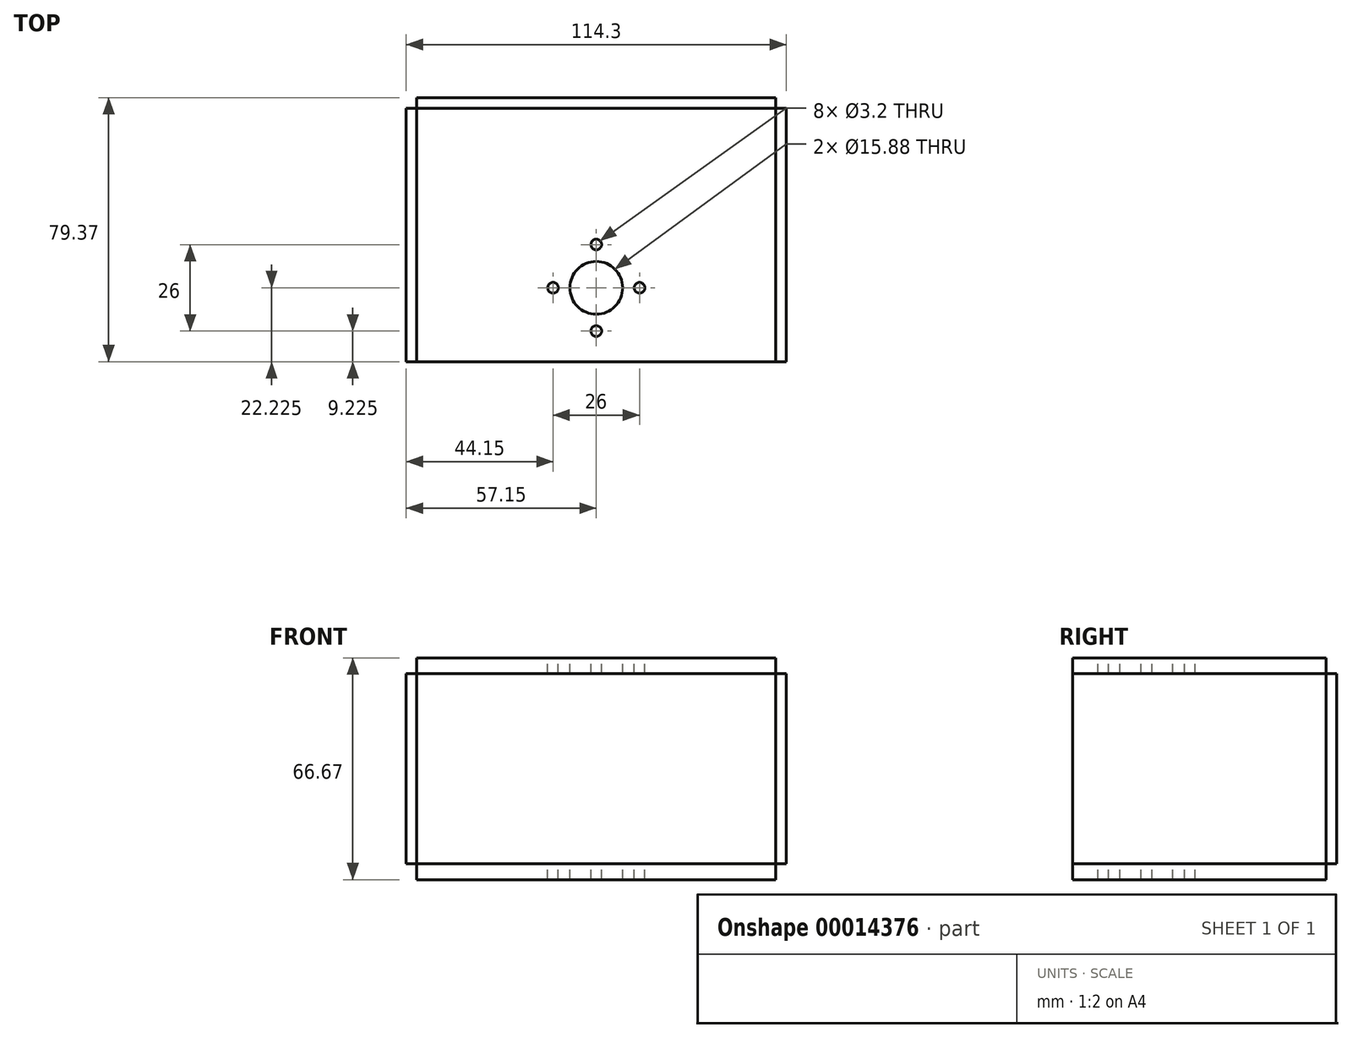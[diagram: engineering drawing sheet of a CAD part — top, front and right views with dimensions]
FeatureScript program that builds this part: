
annotation { "Feature Type Name" : "Feature", "Feature Type Description" : "" }
export const myFeature = defineFeature(function(context is Context, id is Id, definition is map)
    precondition{}
    {
        {
            var Q0;
            Q0=qCreatedBy(makeId("Top.planeOp"),FACE);
            var sketch = newSketch(context, id + "F0", { "sketchPlane" : qUnion([Q0])});
            skLineSegment(sketch, "E0.rect.bottom", {"start": v(53.97, 38.1) * mm, "end": v(-53.98, 38.1) * mm});
            skLineSegment(sketch, "E0.rect.top", {"start": v(53.98, -38.1) * mm, "end": v(-53.97, -38.1) * mm});
            skLineSegment(sketch, "E0.rect.left", {"start": v(53.97, 38.1) * mm, "end": v(53.98, -38.1) * mm});
            skLineSegment(sketch, "E0.rect.right", {"start": v(-53.98, 38.1) * mm, "end": v(-53.97, -38.1) * mm});
            skPoint(sketch, "E0.rect.middle", {"position": v(0, 0) * mm});
            skSolve(sketch);
        }
        {
            var Q0;
            Q0=qSketchRegion(id+"F0",true);
            extrude(context, id + "F1", {"entities" : qUnion([Q0]), "depth" : 4.76 * mm});
        }
        {
            var Q0;
            Q0=makeQuery(id+"F1.opExtrude","SWEPT_FACE",FACE,{"disambiguationData":[OSD([sQuery(id+"F0.wireOp",EDGE,"E0.rect.bottom")])]});
            var sketch = newSketch(context, id + "F2", { "sketchPlane" : qUnion([Q0])});
            skLineSegment(sketch, "E1.bottom", {"start": v(53.98, 0) * mm, "end": v(-53.97, 0) * mm});
            skLineSegment(sketch, "E1.top", {"start": v(53.98, -57.15) * mm, "end": v(-53.97, -57.15) * mm});
            skLineSegment(sketch, "E1.left", {"start": v(53.98, 0) * mm, "end": v(53.98, -57.15) * mm});
            skLineSegment(sketch, "E1.right", {"start": v(-53.97, 0) * mm, "end": v(-53.97, -57.15) * mm});
            skSolve(sketch);
        }
        {
            var Q0;
            Q0=qSketchRegion(id+"F2",true);
            extrude(context, id + "F3", {"entities" : qUnion([Q0]), "depth" : 3.17 * mm});
        }
        {
            var Q0;
            Q0=makeQuery(id+"F1.opExtrude","SWEPT_FACE",FACE,{"disambiguationData":[OSD([sQuery(id+"F0.wireOp",EDGE,"E0.rect.left")])]});
            var sketch = newSketch(context, id + "F4", { "sketchPlane" : qUnion([Q0])});
            skLineSegment(sketch, "E2.bottom", {"start": v(38.1, 0) * mm, "end": v(-38.1, 0) * mm});
            skLineSegment(sketch, "E2.top", {"start": v(38.1, -57.15) * mm, "end": v(-38.1, -57.15) * mm});
            skLineSegment(sketch, "E2.left", {"start": v(38.1, 0) * mm, "end": v(38.1, -57.15) * mm});
            skLineSegment(sketch, "E2.right", {"start": v(-38.1, 0) * mm, "end": v(-38.1, -57.15) * mm});
            skSolve(sketch);
        }
        {
            var Q0;
            Q0=qSketchRegion(id+"F4",true);
            extrude(context, id + "F5", {"entities" : qUnion([Q0]), "depth" : 3.17 * mm});
        }
        {
            var Q0;
            Q0=makeQuery(id+"F5.opExtrude","SWEPT_FACE",FACE,{"disambiguationData":[OSD([sQuery(id+"F4.wireOp",EDGE,"E2.top")])]});
            var sketch = newSketch(context, id + "F6", { "sketchPlane" : qUnion([Q0])});
            skLineSegment(sketch, "E3.bottom", {"start": v(53.97, -38.1) * mm, "end": v(-53.98, -38.1) * mm});
            skLineSegment(sketch, "E3.top", {"start": v(53.98, 38.1) * mm, "end": v(-53.98, 38.1) * mm});
            skLineSegment(sketch, "E3.left", {"start": v(53.97, -38.1) * mm, "end": v(53.97, 38.1) * mm});
            skLineSegment(sketch, "E3.right", {"start": v(-53.98, -38.1) * mm, "end": v(-53.98, 38.1) * mm});
            skSolve(sketch);
        }
        {
            var Q0;
            Q0=qSketchRegion(id+"F6",true);
            extrude(context, id + "F7", {"entities" : qUnion([Q0]), "depth" : 4.76 * mm});
        }
        {
            var Q0;
            Q0=makeQuery(id+"F1.opExtrude","SWEPT_FACE",FACE,{"disambiguationData":[OSD([sQuery(id+"F0.wireOp",EDGE,"E0.rect.right")])]});
            var sketch = newSketch(context, id + "F8", { "sketchPlane" : qUnion([Q0])});
            skLineSegment(sketch, "E4.bottom", {"start": v(-38.1, 0) * mm, "end": v(38.1, 0) * mm});
            skLineSegment(sketch, "E4.top", {"start": v(-38.1, -57.15) * mm, "end": v(38.1, -57.15) * mm});
            skLineSegment(sketch, "E4.left", {"start": v(-38.1, 0) * mm, "end": v(-38.1, -57.15) * mm});
            skLineSegment(sketch, "E4.right", {"start": v(38.1, 0) * mm, "end": v(38.1, -57.15) * mm});
            skSolve(sketch);
        }
        {
            var Q0;
            Q0=qSketchRegion(id+"F8",true);
            extrude(context, id + "F9", {"entities" : qUnion([Q0]), "depth" : 3.17 * mm});
        }
        {
            var Q0;
            Q0=makeQuery(id+"F1.opExtrude","CAP_FACE",FACE,{"disambiguationData":[OSD([sQuery(id+"F0.wireOp",EDGE,"E0.rect.bottom"),sQuery(id+"F0.wireOp",EDGE,"E0.rect.top"),sQuery(id+"F0.wireOp",EDGE,"E0.rect.left"),sQuery(id+"F0.wireOp",EDGE,"E0.rect.right")])],"isStart":false});
            var sketch = newSketch(context, id + "F10", { "sketchPlane" : qUnion([Q0])});
            skLineSegment(sketch, "E5", {"start": v(0, -38.1) * mm, "end": v(0, 38.1) * mm, "construction": true});
            skCircle(sketch, "E6", {"center": v(0, -15.88) * mm, "radius": 7.94 * mm});
            skCircle(sketch, "E7", {"center": v(0, -15.88) * mm, "radius": 13 * mm, "construction": true});
            skCircle(sketch, "E8", {"center": v(13, -15.88) * mm, "radius": 1.6 * mm});
            skCircle(sketch, "E9.1.0", {"center": v(0, -2.88) * mm, "radius": 1.6 * mm});
            skCircle(sketch, "E9.2.0", {"center": v(-13, -15.88) * mm, "radius": 1.6 * mm});
            skCircle(sketch, "E9.3.0", {"center": v(0, -28.87) * mm, "radius": 1.6 * mm});
            skSolve(sketch);
        }
        {
            var Q0;
            Q0=qSketchRegion(id+"F10",true);
            extrude(context, id + "F11", {"entities" : qUnion([Q0]), "operationType" : NewBodyOperationType.REMOVE, "endBound" : BoundingType.THROUGH_ALL, "oppositeDirection" : true, "depth" : 25 * mm});
        }
        {
            var Q0;
            Q0=makeQuery(id+"F7.opExtrude","CAP_FACE",FACE,{"disambiguationData":[OSD([sQuery(id+"F6.wireOp",EDGE,"E3.bottom"),sQuery(id+"F6.wireOp",EDGE,"E3.top"),sQuery(id+"F6.wireOp",EDGE,"E3.left"),sQuery(id+"F6.wireOp",EDGE,"E3.right")])],"isStart":true});
            var sketch = newSketch(context, id + "F12", { "sketchPlane" : qUnion([Q0])});
            skLineSegment(sketch, "E10", {"start": v(0, 38.1) * mm, "end": v(0, -38.1) * mm, "construction": true});
            skCircle(sketch, "E11", {"center": v(0, -15.87) * mm, "radius": 7.94 * mm});
            skCircle(sketch, "E12", {"center": v(0, -15.87) * mm, "radius": 13 * mm, "construction": true});
            skCircle(sketch, "E13", {"center": v(13, -15.87) * mm, "radius": 1.6 * mm});
            skCircle(sketch, "E14.1.0", {"center": v(0, -2.87) * mm, "radius": 1.6 * mm});
            skCircle(sketch, "E14.2.0", {"center": v(-13, -15.87) * mm, "radius": 1.6 * mm});
            skCircle(sketch, "E14.3.0", {"center": v(0, -28.87) * mm, "radius": 1.6 * mm});
            skSolve(sketch);
        }
        {
            var Q0;
            Q0=qSketchRegion(id+"F12",true);
            extrude(context, id + "F13", {"entities" : qUnion([Q0]), "operationType" : NewBodyOperationType.REMOVE, "endBound" : BoundingType.THROUGH_ALL, "oppositeDirection" : true, "depth" : 25.4 * mm});
        }
    });
